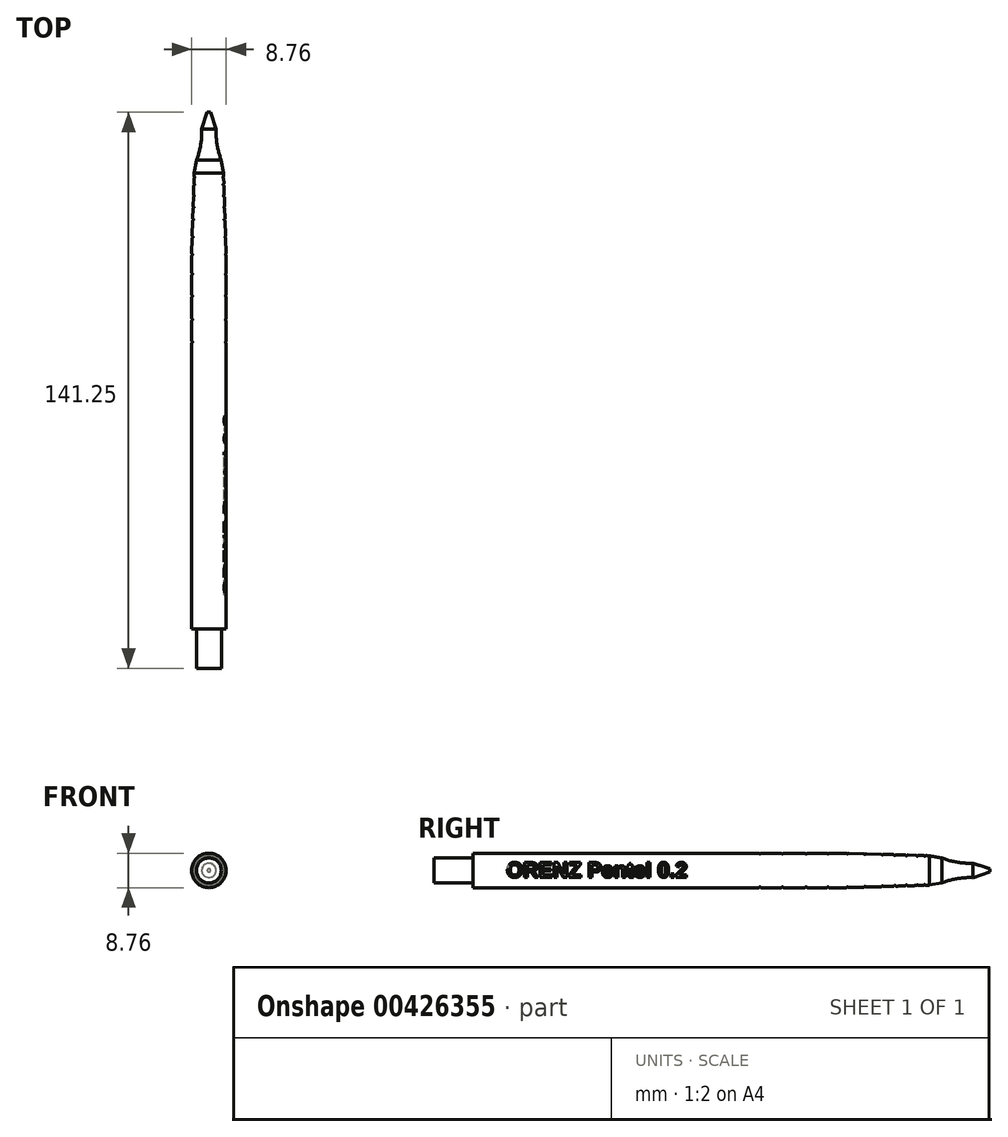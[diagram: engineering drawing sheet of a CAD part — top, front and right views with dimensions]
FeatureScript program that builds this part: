
annotation { "Feature Type Name" : "Feature", "Feature Type Description" : "" }
export const myFeature = defineFeature(function(context is Context, id is Id, definition is map)
    precondition{}
    {
        {
            var Q0;
            Q0=qCreatedBy(makeId("Front.planeOp"),FACE);
            var sketch = newSketch(context, id + "F0", { "sketchPlane" : qUnion([Q0])});
            skCircle(sketch, "E0", {"center": v(0, 0) * mm, "radius": 4.38 * mm});
            skSolve(sketch);
        }
        {
            var Q0;
            Q0 = qSketchRegion(id + "F0", true);
            extrude(context, id + "F1", {"entities" : qUnion([Q0]), "depth" : 95.25 * mm});
        }
        {
            var Q0;
            Q0=makeQuery(id+"F1.opExtrude","CAP_FACE",FACE,{"disambiguationData":[OSD([sQuery(id+"F0.wireOp",EDGE,"E0")])],"isStart":false});
            var sketch = newSketch(context, id + "F2", { "sketchPlane" : qUnion([Q0])});
            skCircle(sketch, "E1", {"center": v(0, 0) * mm, "radius": 3.17 * mm});
            skSolve(sketch);
        }
        {
            var Q0;
            Q0 = qSketchRegion(id + "F2", true);
            extrude(context, id + "F3", {"entities" : qUnion([Q0]), "depth" : 10 * mm});
        }
        {
            var Q0;
            Q0=makeQuery(id+"F1.opExtrude","CAP_FACE",FACE,{"disambiguationData":[OSD([sQuery(id+"F0.wireOp",EDGE,"E0")])],"isStart":true});
            var sketch = newSketch(context, id + "F4", { "sketchPlane" : qUnion([Q0])});
            skCircle(sketch, "E2", {"center": v(0, 0) * mm, "radius": 4.38 * mm});
            skSolve(sketch);
        }
        {
            var Q0;
            Q0 = qSketchRegion(id + "F4", true);
            extrude(context, id + "F5", {"entities" : qUnion([Q0]), "operationType" : NewBodyOperationType.ADD, "depth" : 20.6 * mm, "hasDraft" : true, "draftAngle" : 1.75 * degree, "draftPullDirection" : true});
        }
        {
            var Q0;
            Q0=qCreatedBy(makeId("Right.planeOp"),FACE);
            var sketch = newSketch(context, id + "F6", { "sketchPlane" : qUnion([Q0])});
            skLineSegment(sketch, "E3", {"start": v(20.6, 0) * mm, "end": v(20.6, 3.73) * mm});
            skLineSegment(sketch, "E4", {"start": v(20.6, 3.73) * mm, "end": v(23.9, 3.13) * mm});
            skLineSegment(sketch, "E5", {"start": v(31.7, 1.83) * mm, "end": v(36, 0.43) * mm});
            skLineSegment(sketch, "E6", {"start": v(36, 0.43) * mm, "end": v(36, 0) * mm});
            skLineSegment(sketch, "E7", {"start": v(36, 0) * mm, "end": v(20.6, 0) * mm});
            skArc(sketch, "E8", {"start": v(23.9, 3.13) * mm, "mid": v(27.73, 2.08) * mm, "end": v(31.7, 1.83) * mm});
            skSolve(sketch);
        }
        {
            var Q0;
            Q0 = qSketchRegion(id + "F6", true);
            var Q1;
            Q1=sQuery(id+"F6.wireOp",EDGE,"E7");
            revolve(context, id + "F7", {"entities" : qUnion([Q0]), "axis" : qUnion([Q1]), "revolveType" : RevolveType.FULL});
        }
        {
            var Q0;
            Q0=qCreatedBy(makeId("Right.planeOp"),FACE);
            var sketch = newSketch(context, id + "F8", { "sketchPlane" : qUnion([Q0])});
            skCircle(sketch, "E9", {"center": v(-22.4, 4.37) * mm, "radius": 0.2 * mm});
            skCircle(sketch, "E10", {"center": v(-16.69, 4.38) * mm, "radius": 0.2 * mm});
            skCircle(sketch, "E11", {"center": v(-10.66, 4.38) * mm, "radius": 0.2 * mm});
            skCircle(sketch, "E12", {"center": v(-5.13, 4.38) * mm, "radius": 0.2 * mm});
            skCircle(sketch, "E13", {"center": v(-0.15, 4.38) * mm, "radius": 0.2 * mm});
            skCircle(sketch, "E14", {"center": v(4.3, 4.25) * mm, "radius": 0.2 * mm});
            skCircle(sketch, "E15", {"center": v(8.72, 4.1) * mm, "radius": 0.2 * mm});
            skCircle(sketch, "E16", {"center": v(11.86, 4) * mm, "radius": 0.2 * mm});
            skCircle(sketch, "E17", {"center": v(14.8, 3.9) * mm, "radius": 0.2 * mm});
            skCircle(sketch, "E18", {"center": v(17.6, 3.83) * mm, "radius": 0.2 * mm});
            skCircle(sketch, "E19", {"center": v(19.47, 3.8) * mm, "radius": 0.2 * mm});
            skSolve(sketch);
        }
        {
            var Q0;
            Q0 = qSketchRegion(id + "F8", true);
            var Q1;
            Q1=makeQuery(id+"F5.boolean.opBoolean","MERGE",EDGE,{"derivedFrom":[makeQuery(id+"F1.opExtrude","CAP_EDGE",EDGE,{"disambiguationData":[OSD([sQuery(id+"F0.wireOp",EDGE,"E0")])],"isStart":true}),makeQuery(id+"F5.opExtrude","CAP_EDGE",EDGE,{"disambiguationData":[OSD([sQuery(id+"F4.wireOp",EDGE,"E2")])],"isStart":true})]});
            revolve(context, id + "F9", {"operationType" : NewBodyOperationType.REMOVE, "entities" : qUnion([Q0]), "axis" : qUnion([Q1]), "revolveType" : RevolveType.FULL, "oppositeDirection" : true});
        }
        {
            var Q0;
            Q0=makeQuery(id+"F9.boolean.opBoolean","INTERSECT",EDGE,{"disambiguationData":[OD(0.0)],"derivedFrom":[makeQuery(id+"F1.opExtrude","SWEPT_FACE",FACE,{"disambiguationData":[OSD([sQuery(id+"F0.wireOp",EDGE,"E0")])]}),makeQuery(id+"F9.opRevolve","SWEPT_FACE",FACE,{"disambiguationData":[OSD([sQuery(id+"F8.wireOp",EDGE,"E9")])]})]});
            var Q1;
            Q1=makeQuery(id+"F9.boolean.opBoolean","INTERSECT",EDGE,{"disambiguationData":[OD(1.0)],"derivedFrom":[makeQuery(id+"F1.opExtrude","SWEPT_FACE",FACE,{"disambiguationData":[OSD([sQuery(id+"F0.wireOp",EDGE,"E0")])]}),makeQuery(id+"F9.opRevolve","SWEPT_FACE",FACE,{"disambiguationData":[OSD([sQuery(id+"F8.wireOp",EDGE,"E9")])]})]});
            var Q2;
            Q2=makeQuery(id+"F9.boolean.opBoolean","INTERSECT",EDGE,{"disambiguationData":[OD(0.0)],"derivedFrom":[makeQuery(id+"F1.opExtrude","SWEPT_FACE",FACE,{"disambiguationData":[OSD([sQuery(id+"F0.wireOp",EDGE,"E0")])]}),makeQuery(id+"F9.opRevolve","SWEPT_FACE",FACE,{"disambiguationData":[OSD([sQuery(id+"F8.wireOp",EDGE,"E10")])]})]});
            var Q3;
            Q3=makeQuery(id+"F9.boolean.opBoolean","INTERSECT",EDGE,{"disambiguationData":[OD(1.0)],"derivedFrom":[makeQuery(id+"F1.opExtrude","SWEPT_FACE",FACE,{"disambiguationData":[OSD([sQuery(id+"F0.wireOp",EDGE,"E0")])]}),makeQuery(id+"F9.opRevolve","SWEPT_FACE",FACE,{"disambiguationData":[OSD([sQuery(id+"F8.wireOp",EDGE,"E10")])]})]});
            var Q4;
            Q4=makeQuery(id+"F9.boolean.opBoolean","INTERSECT",EDGE,{"disambiguationData":[OD(0.0)],"derivedFrom":[makeQuery(id+"F1.opExtrude","SWEPT_FACE",FACE,{"disambiguationData":[OSD([sQuery(id+"F0.wireOp",EDGE,"E0")])]}),makeQuery(id+"F9.opRevolve","SWEPT_FACE",FACE,{"disambiguationData":[OSD([sQuery(id+"F8.wireOp",EDGE,"E11")])]})]});
            var Q5;
            Q5=makeQuery(id+"F9.boolean.opBoolean","INTERSECT",EDGE,{"disambiguationData":[OD(1.0)],"derivedFrom":[makeQuery(id+"F1.opExtrude","SWEPT_FACE",FACE,{"disambiguationData":[OSD([sQuery(id+"F0.wireOp",EDGE,"E0")])]}),makeQuery(id+"F9.opRevolve","SWEPT_FACE",FACE,{"disambiguationData":[OSD([sQuery(id+"F8.wireOp",EDGE,"E11")])]})]});
            var Q6;
            Q6=makeQuery(id+"F9.boolean.opBoolean","INTERSECT",EDGE,{"disambiguationData":[OD(0.0)],"derivedFrom":[makeQuery(id+"F1.opExtrude","SWEPT_FACE",FACE,{"disambiguationData":[OSD([sQuery(id+"F0.wireOp",EDGE,"E0")])]}),makeQuery(id+"F9.opRevolve","SWEPT_FACE",FACE,{"disambiguationData":[OSD([sQuery(id+"F8.wireOp",EDGE,"E12")])]})]});
            var Q7;
            Q7=makeQuery(id+"F9.boolean.opBoolean","INTERSECT",EDGE,{"disambiguationData":[OD(1.0)],"derivedFrom":[makeQuery(id+"F1.opExtrude","SWEPT_FACE",FACE,{"disambiguationData":[OSD([sQuery(id+"F0.wireOp",EDGE,"E0")])]}),makeQuery(id+"F9.opRevolve","SWEPT_FACE",FACE,{"disambiguationData":[OSD([sQuery(id+"F8.wireOp",EDGE,"E12")])]})]});
            var Q8;
            Q8=makeQuery(id+"F9.boolean.opBoolean","INTERSECT",EDGE,{"derivedFrom":[makeQuery(id+"F1.opExtrude","SWEPT_FACE",FACE,{"disambiguationData":[OSD([sQuery(id+"F0.wireOp",EDGE,"E0")])]}),makeQuery(id+"F9.opRevolve","SWEPT_FACE",FACE,{"disambiguationData":[OSD([sQuery(id+"F8.wireOp",EDGE,"E13")])]})]});
            var Q9;
            Q9=makeQuery(id+"F9.boolean.opBoolean","INTERSECT",EDGE,{"derivedFrom":[makeQuery(id+"F5.opExtrude","SWEPT_FACE",FACE,{"disambiguationData":[OSD([sQuery(id+"F4.wireOp",EDGE,"E2")])]}),makeQuery(id+"F9.opRevolve","SWEPT_FACE",FACE,{"disambiguationData":[OSD([sQuery(id+"F8.wireOp",EDGE,"E13")])]})]});
            var Q10;
            Q10=makeQuery(id+"F9.boolean.opBoolean","INTERSECT",EDGE,{"disambiguationData":[OD(1.0)],"derivedFrom":[makeQuery(id+"F5.opExtrude","SWEPT_FACE",FACE,{"disambiguationData":[OSD([sQuery(id+"F4.wireOp",EDGE,"E2")])]}),makeQuery(id+"F9.opRevolve","SWEPT_FACE",FACE,{"disambiguationData":[OSD([sQuery(id+"F8.wireOp",EDGE,"E14")])]})]});
            var Q11;
            Q11=makeQuery(id+"F9.boolean.opBoolean","INTERSECT",EDGE,{"disambiguationData":[OD(0.0)],"derivedFrom":[makeQuery(id+"F5.opExtrude","SWEPT_FACE",FACE,{"disambiguationData":[OSD([sQuery(id+"F4.wireOp",EDGE,"E2")])]}),makeQuery(id+"F9.opRevolve","SWEPT_FACE",FACE,{"disambiguationData":[OSD([sQuery(id+"F8.wireOp",EDGE,"E14")])]})]});
            var Q12;
            Q12=makeQuery(id+"F9.boolean.opBoolean","INTERSECT",EDGE,{"disambiguationData":[OD(0.0)],"derivedFrom":[makeQuery(id+"F5.opExtrude","SWEPT_FACE",FACE,{"disambiguationData":[OSD([sQuery(id+"F4.wireOp",EDGE,"E2")])]}),makeQuery(id+"F9.opRevolve","SWEPT_FACE",FACE,{"disambiguationData":[OSD([sQuery(id+"F8.wireOp",EDGE,"E15")])]})]});
            var Q13;
            Q13=makeQuery(id+"F9.boolean.opBoolean","INTERSECT",EDGE,{"disambiguationData":[OD(1.0)],"derivedFrom":[makeQuery(id+"F5.opExtrude","SWEPT_FACE",FACE,{"disambiguationData":[OSD([sQuery(id+"F4.wireOp",EDGE,"E2")])]}),makeQuery(id+"F9.opRevolve","SWEPT_FACE",FACE,{"disambiguationData":[OSD([sQuery(id+"F8.wireOp",EDGE,"E15")])]})]});
            var Q14;
            Q14=makeQuery(id+"F9.boolean.opBoolean","INTERSECT",EDGE,{"disambiguationData":[OD(0.0)],"derivedFrom":[makeQuery(id+"F5.opExtrude","SWEPT_FACE",FACE,{"disambiguationData":[OSD([sQuery(id+"F4.wireOp",EDGE,"E2")])]}),makeQuery(id+"F9.opRevolve","SWEPT_FACE",FACE,{"disambiguationData":[OSD([sQuery(id+"F8.wireOp",EDGE,"E16")])]})]});
            var Q15;
            Q15=makeQuery(id+"F9.boolean.opBoolean","INTERSECT",EDGE,{"disambiguationData":[OD(1.0)],"derivedFrom":[makeQuery(id+"F5.opExtrude","SWEPT_FACE",FACE,{"disambiguationData":[OSD([sQuery(id+"F4.wireOp",EDGE,"E2")])]}),makeQuery(id+"F9.opRevolve","SWEPT_FACE",FACE,{"disambiguationData":[OSD([sQuery(id+"F8.wireOp",EDGE,"E16")])]})]});
            var Q16;
            Q16=makeQuery(id+"F9.boolean.opBoolean","INTERSECT",EDGE,{"disambiguationData":[OD(0.0)],"derivedFrom":[makeQuery(id+"F5.opExtrude","SWEPT_FACE",FACE,{"disambiguationData":[OSD([sQuery(id+"F4.wireOp",EDGE,"E2")])]}),makeQuery(id+"F9.opRevolve","SWEPT_FACE",FACE,{"disambiguationData":[OSD([sQuery(id+"F8.wireOp",EDGE,"E17")])]})]});
            var Q17;
            Q17=makeQuery(id+"F9.boolean.opBoolean","INTERSECT",EDGE,{"disambiguationData":[OD(1.0)],"derivedFrom":[makeQuery(id+"F5.opExtrude","SWEPT_FACE",FACE,{"disambiguationData":[OSD([sQuery(id+"F4.wireOp",EDGE,"E2")])]}),makeQuery(id+"F9.opRevolve","SWEPT_FACE",FACE,{"disambiguationData":[OSD([sQuery(id+"F8.wireOp",EDGE,"E17")])]})]});
            var Q18;
            Q18=makeQuery(id+"F9.boolean.opBoolean","INTERSECT",EDGE,{"disambiguationData":[OD(0.0)],"derivedFrom":[makeQuery(id+"F5.opExtrude","SWEPT_FACE",FACE,{"disambiguationData":[OSD([sQuery(id+"F4.wireOp",EDGE,"E2")])]}),makeQuery(id+"F9.opRevolve","SWEPT_FACE",FACE,{"disambiguationData":[OSD([sQuery(id+"F8.wireOp",EDGE,"E18")])]})]});
            var Q19;
            Q19=makeQuery(id+"F9.boolean.opBoolean","INTERSECT",EDGE,{"disambiguationData":[OD(1.0)],"derivedFrom":[makeQuery(id+"F5.opExtrude","SWEPT_FACE",FACE,{"disambiguationData":[OSD([sQuery(id+"F4.wireOp",EDGE,"E2")])]}),makeQuery(id+"F9.opRevolve","SWEPT_FACE",FACE,{"disambiguationData":[OSD([sQuery(id+"F8.wireOp",EDGE,"E18")])]})]});
            var Q20;
            Q20=makeQuery(id+"F9.boolean.opBoolean","INTERSECT",EDGE,{"disambiguationData":[OD(1.0)],"derivedFrom":[makeQuery(id+"F5.opExtrude","SWEPT_FACE",FACE,{"disambiguationData":[OSD([sQuery(id+"F4.wireOp",EDGE,"E2")])]}),makeQuery(id+"F9.opRevolve","SWEPT_FACE",FACE,{"disambiguationData":[OSD([sQuery(id+"F8.wireOp",EDGE,"E19")])]})]});
            var Q21;
            Q21=makeQuery(id+"F9.boolean.opBoolean","INTERSECT",EDGE,{"disambiguationData":[OD(0.0)],"derivedFrom":[makeQuery(id+"F5.opExtrude","SWEPT_FACE",FACE,{"disambiguationData":[OSD([sQuery(id+"F4.wireOp",EDGE,"E2")])]}),makeQuery(id+"F9.opRevolve","SWEPT_FACE",FACE,{"disambiguationData":[OSD([sQuery(id+"F8.wireOp",EDGE,"E19")])]})]});
            fillet(context, id + "F10", {"entities" : qUnion([Q0, Q1, Q2, Q3, Q4, Q5, Q6, Q7, Q8, Q9, Q10, Q11, Q12, Q13, Q14, Q15, Q16, Q17, Q18, Q19, Q20, Q21]), "radius" : .2 * mm, "tangentPropagation" : true, "allowEdgeOverflow" : false});
        }
        {
            var Q0;
            Q0=qCreatedBy(makeId("Right.planeOp"),FACE);
            cPlane(context, id + "F11", {"entities" : qUnion([Q0]), "cplaneType" : CPlaneType.OFFSET, "offset" : 4.38 * mm, "width" : 150 * mm, "height" : 150 * mm});
        }
        {
            var Q0;
            Q0=qCreatedBy(id+"F11.planeOp",FACE);
            var sketch = newSketch(context, id + "F12", { "sketchPlane" : qUnion([Q0])});
            skText(sketch, "E20", { "text": "ORENZ Pentel 0.2", "fontName": "Arimo-Bold.ttf"});
            const initialGuessF12  = {"E20": [-0.08682, -0.00174, 1, 0, 0.00392]};
            skSetInitialGuess(sketch, initialGuessF12);
            skSolve(sketch);
        }
        {
            var Q0;
            Q0 = qSketchRegion(id + "F12", true);
            extrude(context, id + "F13", {"entities" : qUnion([Q0]), "oppositeDirection" : true, "depth" : .5 * mm});
        }
        {
            var Q0;
            Q0=makeQuery(id+"F1.opExtrude","CAP_FACE",FACE,{"disambiguationData":[OSD([sQuery(id+"F0.wireOp",EDGE,"E0")])],"isStart":false});
            var sketch = newSketch(context, id + "F14", { "sketchPlane" : qUnion([Q0])});
            skCircle(sketch, "E21", {"center": v(0, 0) * mm, "radius": 4.38 * mm});
            skCircle(sketch, "E22", {"center": v(0, 0) * mm, "radius": 6 * mm});
            skSolve(sketch);
        }
        {
            var Q0;
            Q0 = qSketchRegion(id + "F14", true);
            extrude(context, id + "F15", {"entities" : qUnion([Q0]), "operationType" : NewBodyOperationType.REMOVE, "oppositeDirection" : true, "depth" : 100 * mm});
        }
    });
